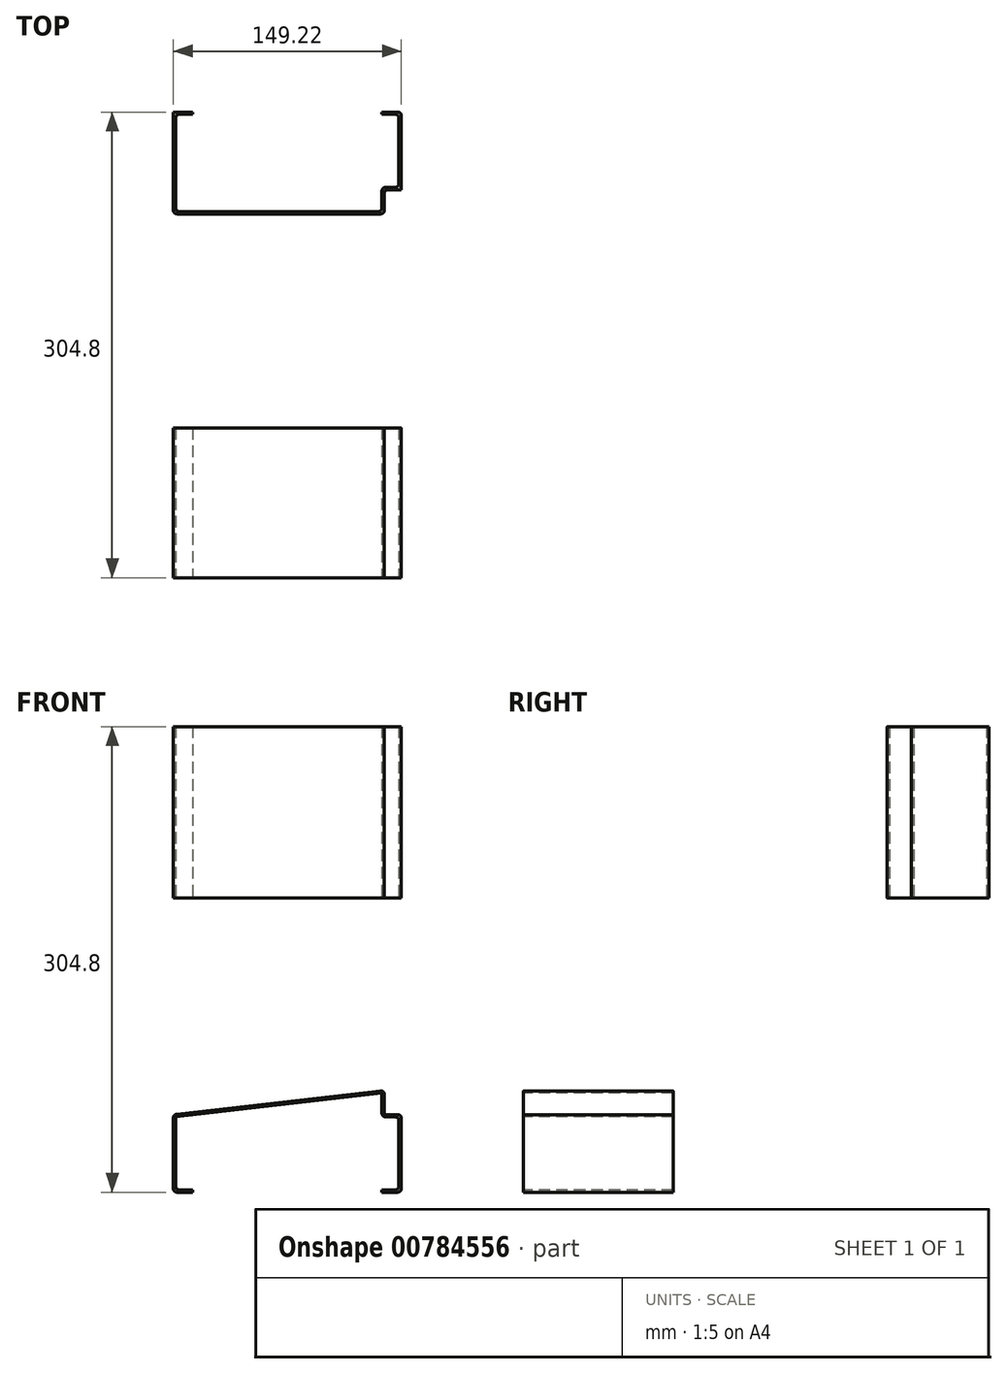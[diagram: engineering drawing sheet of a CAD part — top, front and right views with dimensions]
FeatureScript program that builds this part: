
annotation { "Feature Type Name" : "Feature", "Feature Type Description" : "" }
export const myFeature = defineFeature(function(context is Context, id is Id, definition is map)
    precondition{}
    {
        {
            var Q0;
            Q0=qCreatedBy(makeId("Front.planeOp"),FACE);
            var sketch = newSketch(context, id + "F0", { "sketchPlane" : qUnion([Q0])});
            skLineSegment(sketch, "E0", {"start": v(-61.91, -50.8) * mm, "end": v(-74.61, -50.8) * mm});
            skLineSegment(sketch, "E1", {"start": v(-74.61, -50.8) * mm, "end": v(-74.61, 0) * mm});
            skLineSegment(sketch, "E2", {"start": v(-74.61, 0) * mm, "end": v(63.5, 15.87) * mm});
            skLineSegment(sketch, "E3", {"start": v(63.5, 15.87) * mm, "end": v(63.5, 0) * mm});
            skLineSegment(sketch, "E4", {"start": v(63.5, 0) * mm, "end": v(74.61, 0) * mm});
            skLineSegment(sketch, "E5", {"start": v(74.61, 0) * mm, "end": v(74.61, -50.8) * mm});
            skLineSegment(sketch, "E6", {"start": v(74.61, -50.8) * mm, "end": v(61.91, -50.8) * mm});
            skLineSegment(sketch, "E7", {"start": v(-61.91, -50.8) * mm, "end": v(0, -50.8) * mm, "construction": true});
            skLineSegment(sketch, "E8", {"start": v(0, -50.8) * mm, "end": v(61.91, -50.8) * mm, "construction": true});
            skLineSegment(sketch, "E9.0", {"start": v(73.09, -49.28) * mm, "end": v(61.91, -49.28) * mm});
            skLineSegment(sketch, "E9.1", {"start": v(73.09, -1.52) * mm, "end": v(73.09, -49.28) * mm});
            skLineSegment(sketch, "E9.2", {"start": v(61.98, -1.52) * mm, "end": v(73.09, -1.52) * mm});
            skLineSegment(sketch, "E9.3", {"start": v(-61.91, -49.28) * mm, "end": v(-73.09, -49.28) * mm});
            skLineSegment(sketch, "E9.4", {"start": v(-73.09, -49.28) * mm, "end": v(-73.09, -1.36) * mm});
            skLineSegment(sketch, "E9.5", {"start": v(-73.09, -1.36) * mm, "end": v(61.98, 14.17) * mm});
            skLineSegment(sketch, "E9.6", {"start": v(61.98, 14.17) * mm, "end": v(61.98, -1.52) * mm});
            skLineSegment(sketch, "E10", {"start": v(-61.91, -49.28) * mm, "end": v(-61.91, -50.8) * mm});
            skLineSegment(sketch, "E11", {"start": v(61.91, -50.8) * mm, "end": v(61.91, -49.28) * mm});
            skSolve(sketch);
        }
        {
            var Q0;
            Q0=qSketchRegion(id+"F0",true);
            extrude(context, id + "F1", {"entities" : qUnion([Q0]), "oppositeDirection" : true, "depth" : 304.8 * mm, "offsetDistance" : 25.4 * mm});
        }
        {
            var Q0;
            Q0=qCreatedBy(makeId("Top.planeOp"),FACE);
            var sketch = newSketch(context, id + "F2", { "sketchPlane" : qUnion([Q0])});
            skPoint(sketch, "E12.0", {"position": v(-74.61, 304.8) * mm});
            skPoint(sketch, "E13.0", {"position": v(74.61, 304.8) * mm});
            skPoint(sketch, "E14.0", {"position": v(61.98, 304.8) * mm});
            skLineSegment(sketch, "E15", {"start": v(-74.61, 304.8) * mm, "end": v(-74.61, 238.12) * mm});
            skLineSegment(sketch, "E16", {"start": v(-74.61, 238.12) * mm, "end": v(63.5, 238.13) * mm});
            skLineSegment(sketch, "E17", {"start": v(63.5, 254) * mm, "end": v(74.61, 254) * mm});
            skLineSegment(sketch, "E18", {"start": v(74.61, 254) * mm, "end": v(74.61, 304.8) * mm});
            skLineSegment(sketch, "E19", {"start": v(61.98, 304.8) * mm, "end": v(74.61, 304.8) * mm});
            skLineSegment(sketch, "E20", {"start": v(-74.61, 304.8) * mm, "end": v(-61.91, 304.8) * mm});
            skLineSegment(sketch, "E21.0", {"start": v(-73.09, 303.28) * mm, "end": v(-61.91, 303.28) * mm});
            skLineSegment(sketch, "E21.1", {"start": v(-73.09, 303.28) * mm, "end": v(-73.09, 239.65) * mm});
            skLineSegment(sketch, "E21.2", {"start": v(-73.09, 239.65) * mm, "end": v(61.98, 239.65) * mm});
            skLineSegment(sketch, "E21.3", {"start": v(61.98, 303.28) * mm, "end": v(73.09, 303.28) * mm});
            skLineSegment(sketch, "E21.4", {"start": v(73.09, 255.52) * mm, "end": v(73.09, 303.28) * mm});
            skLineSegment(sketch, "E21.5", {"start": v(61.98, 255.52) * mm, "end": v(73.09, 255.52) * mm});
            skLineSegment(sketch, "E21.6", {"start": v(61.98, 239.65) * mm, "end": v(61.98, 255.52) * mm});
            skLineSegment(sketch, "E22", {"start": v(-61.91, 304.8) * mm, "end": v(-61.91, 303.28) * mm});
            skLineSegment(sketch, "E23", {"start": v(61.98, 304.8) * mm, "end": v(61.98, 303.28) * mm});
            skLineSegment(sketch, "E24", {"start": v(63.5, 238.13) * mm, "end": v(63.5, 254) * mm});
            skSolve(sketch);
        }
        {
            var Q0;
            Q0=qSketchRegion(id+"F2",true);
            extrude(context, id + "F3", {"entities" : qUnion([Q0]), "depth" : 254 * mm, "offsetDistance" : 25.4 * mm, "hasSecondDirection" : true, "secondDirectionOppositeDirection" : true, "secondDirectionDepth" : 50.8 * mm});
        }
        {
            var Q0;
            Q0=makeQuery(id+"F1.opExtrude","SWEPT_BODY",BODY,{"disambiguationData":[OSD([sQuery(id+"F0.wireOp",EDGE,"E0"),sQuery(id+"F0.wireOp",EDGE,"E1"),sQuery(id+"F0.wireOp",EDGE,"E2"),sQuery(id+"F0.wireOp",EDGE,"E3"),sQuery(id+"F0.wireOp",EDGE,"E4"),sQuery(id+"F0.wireOp",EDGE,"E5"),sQuery(id+"F0.wireOp",EDGE,"E6"),sQuery(id+"F0.wireOp",EDGE,"E9.0"),sQuery(id+"F0.wireOp",EDGE,"E9.1"),sQuery(id+"F0.wireOp",EDGE,"E9.2"),sQuery(id+"F0.wireOp",EDGE,"E9.3"),sQuery(id+"F0.wireOp",EDGE,"E9.4"),sQuery(id+"F0.wireOp",EDGE,"E9.5"),sQuery(id+"F0.wireOp",EDGE,"E9.6"),sQuery(id+"F0.wireOp",EDGE,"E10"),sQuery(id+"F0.wireOp",EDGE,"E11")])]});
            var Q1;
            Q1=makeQuery(id+"F3.opExtrude","SWEPT_BODY",BODY,{"disambiguationData":[OSD([sQuery(id+"F2.wireOp",EDGE,"E15"),sQuery(id+"F2.wireOp",EDGE,"E16"),sQuery(id+"F2.wireOp",EDGE,"vNE0MKmX-Wy9i-YOhV-lQRx-KuhJFtJfketY"),sQuery(id+"F2.wireOp",EDGE,"E17"),sQuery(id+"F2.wireOp",EDGE,"E18"),sQuery(id+"F2.wireOp",EDGE,"E19"),sQuery(id+"F2.wireOp",EDGE,"E20"),sQuery(id+"F2.wireOp",EDGE,"E21.0"),sQuery(id+"F2.wireOp",EDGE,"E21.1"),sQuery(id+"F2.wireOp",EDGE,"E21.2"),sQuery(id+"F2.wireOp",EDGE,"E21.3"),sQuery(id+"F2.wireOp",EDGE,"E21.4"),sQuery(id+"F2.wireOp",EDGE,"E21.5"),sQuery(id+"F2.wireOp",EDGE,"E21.6"),sQuery(id+"F2.wireOp",EDGE,"E22"),sQuery(id+"F2.wireOp",EDGE,"E23")])]});
            booleanBodies(context, id + "F4", {"operationType" : BooleanOperationType.INTERSECTION, "tools" : qUnion([Q0, Q1]), "keepTools" : true});
        }
        {
            var Q0;
            Q0=makeQuery(id+"F3.opExtrude","SWEPT_FACE",FACE,{"disambiguationData":[OSD([sQuery(id+"F2.wireOp",EDGE,"E16")])]});
            var sketch = newSketch(context, id + "F5", { "sketchPlane" : qUnion([Q0])});
            skPoint(sketch, "E25.0", {"position": v(61.98, 14.17) * mm});
            skPoint(sketch, "E26.0", {"position": v(-73.09, -1.36) * mm});
            skLineSegment(sketch, "E27", {"start": v(-73.09, -1.36) * mm, "end": v(61.98, 14.17) * mm});
            skLineSegment(sketch, "E28", {"start": v(-73.09, -1.36) * mm, "end": v(-91.14, -3.43) * mm});
            skPoint(sketch, "E29.0", {"position": v(61.98, 0) * mm});
            skLineSegment(sketch, "E30", {"start": v(61.98, 14.17) * mm, "end": v(61.98, 0) * mm});
            skLineSegment(sketch, "E31", {"start": v(61.98, 0) * mm, "end": v(86.32, 0) * mm});
            skLineSegment(sketch, "E32", {"start": v(-91.14, -3.43) * mm, "end": v(-91.14, -71.1) * mm});
            skLineSegment(sketch, "E33", {"start": v(-91.14, -71.1) * mm, "end": v(86.32, -71.1) * mm});
            skLineSegment(sketch, "E34", {"start": v(86.32, -71.1) * mm, "end": v(86.32, 0) * mm});
            skPoint(sketch, "E35.0", {"position": v(63.5, 0) * mm});
            skSolve(sketch);
        }
        {
            var Q0;
            Q0=qSketchRegion(id+"F5",true);
            var Q1;
            Q1=makeQuery(id+"F3.opExtrude","SWEPT_FACE",FACE,{"disambiguationData":[OSD([sQuery(id+"F2.wireOp",EDGE,"E17")])]});
            extrude(context, id + "F6", {"entities" : qUnion([Q0]), "operationType" : NewBodyOperationType.REMOVE, "endBound" : BoundingType.UP_TO_SURFACE, "oppositeDirection" : true, "depth" : 25.4 * mm, "endBoundEntityFace" : qUnion([Q1]), "offsetDistance" : 25.4 * mm});
        }
        {
            var Q0;
            Q0=makeQuery(id+"F3.opExtrude","SWEPT_FACE",FACE,{"disambiguationData":[OSD([sQuery(id+"F2.wireOp",EDGE,"E16")])]});
            var sketch = newSketch(context, id + "F7", { "sketchPlane" : qUnion([Q0])});
            skPoint(sketch, "E36.0", {"position": v(-74.61, -1.53) * mm});
            skPoint(sketch, "E37.0", {"position": v(63.5, 0) * mm});
            skPoint(sketch, "E38.0", {"position": v(61.98, 0) * mm});
            skPoint(sketch, "E39.0", {"position": v(63.5, 15.87) * mm});
            skPoint(sketch, "E40.0", {"position": v(-74.61, 0) * mm});
            skPoint(sketch, "E41.0", {"position": v(-73.09, -1.36) * mm});
            skPoint(sketch, "E42.0", {"position": v(61.98, 14.17) * mm});
            skLineSegment(sketch, "E43", {"start": v(-74.61, -1.53) * mm, "end": v(61.98, 14.17) * mm});
            skLineSegment(sketch, "E44", {"start": v(61.98, 14.17) * mm, "end": v(61.98, 0) * mm});
            skLineSegment(sketch, "E45", {"start": v(61.98, 0) * mm, "end": v(63.5, 0) * mm});
            skLineSegment(sketch, "E46", {"start": v(63.5, 0) * mm, "end": v(63.5, 15.87) * mm});
            skLineSegment(sketch, "E47", {"start": v(63.5, 15.87) * mm, "end": v(-74.61, 0) * mm});
            skLineSegment(sketch, "E48", {"start": v(-74.61, 0) * mm, "end": v(-74.61, -1.53) * mm});
            skSolve(sketch);
        }
        {
            var Q0;
            Q0=qSketchRegion(id+"F7",true);
            extrude(context, id + "F8", {"entities" : qUnion([Q0]), "operationType" : NewBodyOperationType.REMOVE, "endBound" : BoundingType.THROUGH_ALL, "oppositeDirection" : true, "depth" : 25.4 * mm, "offsetDistance" : 25.4 * mm});
        }
        {
            var Q0;
            Q0=makeQuery(id+"F4.opBoolean","INTERSECT",BODY,{"derivedFrom":[makeQuery(id+"F1.opExtrude","SWEPT_BODY",BODY,{"disambiguationData":[OSD([sQuery(id+"F0.wireOp",EDGE,"E0"),sQuery(id+"F0.wireOp",EDGE,"E1"),sQuery(id+"F0.wireOp",EDGE,"E2"),sQuery(id+"F0.wireOp",EDGE,"E3"),sQuery(id+"F0.wireOp",EDGE,"E4"),sQuery(id+"F0.wireOp",EDGE,"E5"),sQuery(id+"F0.wireOp",EDGE,"E6"),sQuery(id+"F0.wireOp",EDGE,"E9.0"),sQuery(id+"F0.wireOp",EDGE,"E9.1"),sQuery(id+"F0.wireOp",EDGE,"E9.2"),sQuery(id+"F0.wireOp",EDGE,"E9.3"),sQuery(id+"F0.wireOp",EDGE,"E9.4"),sQuery(id+"F0.wireOp",EDGE,"E9.5"),sQuery(id+"F0.wireOp",EDGE,"E9.6"),sQuery(id+"F0.wireOp",EDGE,"E10"),sQuery(id+"F0.wireOp",EDGE,"E11")])]}),makeQuery(id+"F3.opExtrude","SWEPT_BODY",BODY,{"disambiguationData":[OSD([sQuery(id+"F2.wireOp",EDGE,"E15"),sQuery(id+"F2.wireOp",EDGE,"E16"),sQuery(id+"F2.wireOp",EDGE,"E17"),sQuery(id+"F2.wireOp",EDGE,"E18"),sQuery(id+"F2.wireOp",EDGE,"E19"),sQuery(id+"F2.wireOp",EDGE,"E20"),sQuery(id+"F2.wireOp",EDGE,"E21.0"),sQuery(id+"F2.wireOp",EDGE,"E21.1"),sQuery(id+"F2.wireOp",EDGE,"E21.2"),sQuery(id+"F2.wireOp",EDGE,"E21.3"),sQuery(id+"F2.wireOp",EDGE,"E21.4"),sQuery(id+"F2.wireOp",EDGE,"E21.5"),sQuery(id+"F2.wireOp",EDGE,"E21.6"),sQuery(id+"F2.wireOp",EDGE,"E22"),sQuery(id+"F2.wireOp",EDGE,"E23"),sQuery(id+"F2.wireOp",EDGE,"E24")])]})]});
            deleteBodies(context, id + "F9", {"entities" : qUnion([Q0])});
        }
        {
            var Q0;
            Q0=makeQuery(id+"F1.opExtrude","SWEPT_BODY",BODY,{"disambiguationData":[OSD([sQuery(id+"F0.wireOp",EDGE,"E0"),sQuery(id+"F0.wireOp",EDGE,"E1"),sQuery(id+"F0.wireOp",EDGE,"E2"),sQuery(id+"F0.wireOp",EDGE,"E3"),sQuery(id+"F0.wireOp",EDGE,"E4"),sQuery(id+"F0.wireOp",EDGE,"E5"),sQuery(id+"F0.wireOp",EDGE,"E6"),sQuery(id+"F0.wireOp",EDGE,"E9.0"),sQuery(id+"F0.wireOp",EDGE,"E9.1"),sQuery(id+"F0.wireOp",EDGE,"E9.2"),sQuery(id+"F0.wireOp",EDGE,"E9.3"),sQuery(id+"F0.wireOp",EDGE,"E9.4"),sQuery(id+"F0.wireOp",EDGE,"E9.5"),sQuery(id+"F0.wireOp",EDGE,"E9.6"),sQuery(id+"F0.wireOp",EDGE,"E10"),sQuery(id+"F0.wireOp",EDGE,"E11")])]});
            var Q1;
            Q1=makeQuery(id+"F3.opExtrude","SWEPT_BODY",BODY,{"disambiguationData":[OSD([sQuery(id+"F2.wireOp",EDGE,"E15"),sQuery(id+"F2.wireOp",EDGE,"E16"),sQuery(id+"F2.wireOp",EDGE,"E17"),sQuery(id+"F2.wireOp",EDGE,"E18"),sQuery(id+"F2.wireOp",EDGE,"E19"),sQuery(id+"F2.wireOp",EDGE,"E20"),sQuery(id+"F2.wireOp",EDGE,"E21.0"),sQuery(id+"F2.wireOp",EDGE,"E21.1"),sQuery(id+"F2.wireOp",EDGE,"E21.2"),sQuery(id+"F2.wireOp",EDGE,"E21.3"),sQuery(id+"F2.wireOp",EDGE,"E21.4"),sQuery(id+"F2.wireOp",EDGE,"E21.5"),sQuery(id+"F2.wireOp",EDGE,"E21.6"),sQuery(id+"F2.wireOp",EDGE,"E22"),sQuery(id+"F2.wireOp",EDGE,"E23"),sQuery(id+"F2.wireOp",EDGE,"E24")])]});
            booleanBodies(context, id + "F10", {"operationType" : BooleanOperationType.UNION, "tools" : qUnion([Q0, Q1])});
        }
        {
            var Q0;
            {var subQ0=sQuery(id+"F0.wireOp",EDGE,"E3");var subQ2=sQuery(id+"F0.wireOp",EDGE,"E4");Q0=makeQuery(id+"F10.opBoolean","SPLIT",FACE,{"disambiguationData":[TD([makeQuery(id+"F1.opExtrude","SWEPT_FACE",FACE,{"disambiguationData":[OSD([subQ0])]})])],"derivedFrom":makeQuery(id+"F8.boolean.opBoolean","MERGE",FACE,{"derivedFrom":[makeQuery(id+"F1.opExtrude","SWEPT_FACE",FACE,{"disambiguationData":[OSD([subQ2])]})],"fromTools":[makeQuery(id+"F8.opExtrude","SWEPT_FACE",FACE,{"disambiguationData":[OSD([sQuery(id+"F7.wireOp",EDGE,"E45")])]})]})});}
            var sketch = newSketch(context, id + "F11", { "sketchPlane" : qUnion([Q0])});
            skPoint(sketch, "E49.0", {"position": v(63.5, 238.13) * mm});
            skLineSegment(sketch, "E50.bottom", {"start": v(63.5, 238.13) * mm, "end": v(61.37, 238.13) * mm});
            skLineSegment(sketch, "E50.top", {"start": v(63.5, 238.07) * mm, "end": v(61.37, 238.07) * mm});
            skLineSegment(sketch, "E50.left", {"start": v(63.5, 238.13) * mm, "end": v(63.5, 238.07) * mm});
            skLineSegment(sketch, "E50.right", {"start": v(61.37, 238.13) * mm, "end": v(61.37, 238.07) * mm});
            skSolve(sketch);
        }
        {
            var Q0;
            Q0=qSketchRegion(id+"F11",true);
            extrude(context, id + "F12", {"entities" : qUnion([Q0]), "operationType" : NewBodyOperationType.REMOVE, "endBound" : BoundingType.THROUGH_ALL, "depth" : 25.4 * mm, "offsetDistance" : 25.4 * mm});
        }
        {
            var Q0;
            Q0=qCreatedBy(makeId("Right.planeOp"),FACE);
            var sketch = newSketch(context, id + "F13", { "sketchPlane" : qUnion([Q0])});
            skLineSegment(sketch, "E51.bottom", {"start": v(97.94, 141.78) * mm, "end": v(397.03, 141.78) * mm});
            skLineSegment(sketch, "E51.top", {"start": v(97.94, -138.25) * mm, "end": v(397.03, -138.25) * mm});
            skLineSegment(sketch, "E51.left", {"start": v(97.94, 141.78) * mm, "end": v(97.94, -138.25) * mm});
            skLineSegment(sketch, "E51.right", {"start": v(397.03, 141.78) * mm, "end": v(397.03, -138.25) * mm});
            skSolve(sketch);
        }
        {
            var Q0;
            Q0 = qSketchRegion(id + "F13", true);
            extrude(context, id + "F14", {"entities" : qUnion([Q0]), "operationType" : NewBodyOperationType.REMOVE, "endBound" : BoundingType.THROUGH_ALL, "oppositeDirection" : true, "depth" : 25.4 * mm, "offsetDistance" : 25.4 * mm, "hasSecondDirection" : true, "secondDirectionBound" : BoundingType.THROUGH_ALL, "secondDirectionOppositeDirection" : false, "secondDirectionDepth" : 25.4 * mm});
        }
        {
            var Q0;
            Q0=makeQuery(id+"F3.opExtrude","SWEPT_EDGE",EDGE,{"disambiguationData":[OSD([sQuery(id+"F2.wireOp",EDGE,"E21.1"),sQuery(id+"F2.wireOp",EDGE,"E21.2")])]});
            var Q1;
            Q1=makeQuery(id+"F3.opExtrude","SWEPT_EDGE",EDGE,{"disambiguationData":[OSD([sQuery(id+"F2.wireOp",EDGE,"E15"),sQuery(id+"F2.wireOp",EDGE,"E16")])]});
            var Q2;
            Q2=makeQuery(id+"F10.opBoolean","MERGE",EDGE,{"derivedFrom":[makeQuery(id+"F3.opExtrude","SWEPT_EDGE",EDGE,{"disambiguationData":[OSD([sQuery(id+"F2.wireOp",EDGE,"E15"),sQuery(id+"F2.wireOp",EDGE,"E20")])]}),makeQuery(id+"F1.opExtrude","CAP_EDGE",EDGE,{"disambiguationData":[OSD([sQuery(id+"F0.wireOp",EDGE,"E1")])],"isStart":false})]});
            var Q3;
            Q3=makeQuery(id+"F3.opExtrude","SWEPT_EDGE",EDGE,{"disambiguationData":[OSD([sQuery(id+"F2.wireOp",EDGE,"E21.0"),sQuery(id+"F2.wireOp",EDGE,"E21.1")])]});
            var Q4;
            Q4=makeQuery(id+"F3.opExtrude","SWEPT_EDGE",EDGE,{"disambiguationData":[OSD([sQuery(id+"F2.wireOp",EDGE,"E21.2"),sQuery(id+"F2.wireOp",EDGE,"E21.6")])]});
            var Q5;
            {var subQ1=sQuery(id+"F2.wireOp",EDGE,"E21.6");var subQ2=sQuery(id+"F2.wireOp",EDGE,"E21.5");Q5=makeQuery(id+"F10.opBoolean","SPLIT",EDGE,{"disambiguationData":[TD([makeQuery(id+"F1.opExtrude","SWEPT_FACE",FACE,{"disambiguationData":[OSD([sQuery(id+"F0.wireOp",EDGE,"E4")])]})])],"derivedFrom":makeQuery(id+"F3.opExtrude","SWEPT_EDGE",EDGE,{"disambiguationData":[OSD([subQ2,subQ1])]})});}
            var Q6;
            {var subQ0=sQuery(id+"F2.wireOp",EDGE,"E21.4");var subQ1=sQuery(id+"F2.wireOp",EDGE,"E21.5");Q6=makeQuery(id+"F10.opBoolean","SPLIT",EDGE,{"disambiguationData":[topologyDisambiguationEdgeConnected([makeQuery(id+"F3.opExtrude","SWEPT_FACE",FACE,{"disambiguationData":[OSD([subQ0])]})])],"derivedFrom":makeQuery(id+"F3.opExtrude","SWEPT_EDGE",EDGE,{"disambiguationData":[OSD([subQ0,subQ1])]})});}
            var Q7;
            {var subQ0=sQuery(id+"F2.wireOp",EDGE,"E21.3");var subQ1=sQuery(id+"F2.wireOp",EDGE,"E21.4");Q7=makeQuery(id+"F10.opBoolean","SPLIT",EDGE,{"disambiguationData":[topologyDisambiguationEdgeConnected([makeQuery(id+"F3.opExtrude","SWEPT_FACE",FACE,{"disambiguationData":[OSD([subQ1])]})])],"derivedFrom":makeQuery(id+"F3.opExtrude","SWEPT_EDGE",EDGE,{"disambiguationData":[OSD([subQ0,subQ1])]})});}
            var Q8;
            {var subQ0=sQuery(id+"F2.wireOp",EDGE,"E24");Q8=makeQuery(id+"F12.boolean.opBoolean","MERGE",EDGE,{"derivedFrom":[makeQuery(id+"F3.opExtrude","SWEPT_EDGE",EDGE,{"disambiguationData":[OSD([sQuery(id+"F2.wireOp",EDGE,"E16"),subQ0])]})],"fromTools":[makeQuery(id+"F12.opExtrude","SWEPT_EDGE",EDGE,{"disambiguationData":[OSD([sQuery(id+"F0.wireOp",EDGE,"E3"),sQuery(id+"F0.wireOp",EDGE,"E4"),subQ0,sQuery(id+"F5.wireOp",EDGE,"E31"),sQuery(id+"F11.wireOp",EDGE,"E50.bottom"),sQuery(id+"F11.wireOp",EDGE,"E50.left")])]})]});}
            var Q9;
            Q9=makeQuery(id+"F3.opExtrude","SWEPT_EDGE",EDGE,{"disambiguationData":[OSD([sQuery(id+"F2.wireOp",EDGE,"E17"),sQuery(id+"F2.wireOp",EDGE,"E24")])]});
            var Q10;
            Q10=makeQuery(id+"F3.opExtrude","SWEPT_EDGE",EDGE,{"disambiguationData":[OSD([sQuery(id+"F2.wireOp",EDGE,"E17"),sQuery(id+"F2.wireOp",EDGE,"E18")])]});
            var Q11;
            Q11=makeQuery(id+"F10.opBoolean","MERGE",EDGE,{"derivedFrom":[makeQuery(id+"F1.opExtrude","CAP_EDGE",EDGE,{"disambiguationData":[OSD([sQuery(id+"F0.wireOp",EDGE,"E5")])],"isStart":false}),makeQuery(id+"F3.opExtrude","SWEPT_EDGE",EDGE,{"disambiguationData":[OSD([sQuery(id+"F2.wireOp",EDGE,"E18"),sQuery(id+"F2.wireOp",EDGE,"E19")])]})]});
            fillet(context, id + "F15", {"entities" : qUnion([Q0, Q1, Q2, Q3, Q4, Q5, Q6, Q7, Q8, Q9, Q10, Q11]), "radius" : 2.38 * mm, "tangentPropagation" : true, "allowEdgeOverflow" : false});
        }
        {
            var Q0;
            Q0=makeQuery(id+"F1.opExtrude","SWEPT_EDGE",EDGE,{"disambiguationData":[OSD([sQuery(id+"F0.wireOp",EDGE,"E9.3"),sQuery(id+"F0.wireOp",EDGE,"E9.4")])]});
            var Q1;
            {var subQ0=sQuery(id+"F0.wireOp",EDGE,"E9.4");var subQ2=sQuery(id+"F0.wireOp",EDGE,"E9.5");var subQ3=makeQuery(id+"F1.opExtrude","SWEPT_EDGE",EDGE,{"disambiguationData":[OSD([subQ0,subQ2])]});Q1=makeQuery(id+"F10.opBoolean","MERGE",EDGE,{"derivedFrom":[makeQuery(id+"F8.boolean.opBoolean","SPLIT",EDGE,{"disambiguationData":[topologyDisambiguationEdgeConnected([makeQuery(id+"F1.opExtrude","SWEPT_FACE",FACE,{"disambiguationData":[OSD([subQ2])]})])],"derivedFrom":subQ3}),makeQuery(id+"F8.boolean.opBoolean","SPLIT",EDGE,{"disambiguationData":[topologyDisambiguationEdgeConnected([makeQuery(id+"F8.opExtrude","SWEPT_FACE",FACE,{"disambiguationData":[OSD([sQuery(id+"F7.wireOp",EDGE,"E43")])]})])],"derivedFrom":subQ3})]});}
            var Q2;
            {var subQ0=sQuery(id+"F0.wireOp",EDGE,"E9.6");var subQ1=sQuery(id+"F0.wireOp",EDGE,"E9.5");var subQ2=sQuery(id+"F5.wireOp",EDGE,"E27");Q2=makeQuery(id+"F12.boolean.opBoolean","SPLIT",EDGE,{"disambiguationData":[TD([makeQuery(id+"F12.opExtrude","SWEPT_FACE",FACE,{"disambiguationData":[OSD([sQuery(id+"F11.wireOp",EDGE,"E50.top")])]})])],"derivedFrom":makeQuery(id+"F10.opBoolean","MERGE",EDGE,{"derivedFrom":[makeQuery(id+"F6.boolean.opBoolean","COPY",EDGE,{"derivedFrom":makeQuery(id+"F6.opExtrude","SWEPT_EDGE",EDGE,{"disambiguationData":[OSD([subQ2,sQuery(id+"F5.wireOp",EDGE,"E30")])]})}),makeQuery(id+"F1.opExtrude","SWEPT_EDGE",EDGE,{"disambiguationData":[OSD([subQ1,subQ0])]})]})});}
            var Q3;
            {var subQ0=sQuery(id+"F0.wireOp",EDGE,"E9.6");var subQ1=sQuery(id+"F0.wireOp",EDGE,"E9.2");Q3=makeQuery(id+"F10.opBoolean","SPLIT",EDGE,{"disambiguationData":[TD([makeQuery(id+"F3.opExtrude","SWEPT_FACE",FACE,{"disambiguationData":[OSD([sQuery(id+"F2.wireOp",EDGE,"E17")])]})])],"derivedFrom":makeQuery(id+"F1.opExtrude","SWEPT_EDGE",EDGE,{"disambiguationData":[OSD([subQ1,subQ0])]})});}
            var Q4;
            {var subQ0=sQuery(id+"F0.wireOp",EDGE,"E9.2");var subQ1=sQuery(id+"F0.wireOp",EDGE,"E9.1");Q4=makeQuery(id+"F10.opBoolean","SPLIT",EDGE,{"disambiguationData":[TD([makeQuery(id+"F3.opExtrude","SWEPT_FACE",FACE,{"disambiguationData":[OSD([sQuery(id+"F2.wireOp",EDGE,"E17")])]})])],"derivedFrom":makeQuery(id+"F1.opExtrude","SWEPT_EDGE",EDGE,{"disambiguationData":[OSD([subQ1,subQ0])]})});}
            var Q5;
            {var subQ0=sQuery(id+"F0.wireOp",EDGE,"E9.1");var subQ1=sQuery(id+"F0.wireOp",EDGE,"E9.0");Q5=makeQuery(id+"F10.opBoolean","SPLIT",EDGE,{"disambiguationData":[TD([makeQuery(id+"F3.opExtrude","SWEPT_FACE",FACE,{"disambiguationData":[OSD([sQuery(id+"F2.wireOp",EDGE,"E17")])]})])],"derivedFrom":makeQuery(id+"F1.opExtrude","SWEPT_EDGE",EDGE,{"disambiguationData":[OSD([subQ1,subQ0])]})});}
            var Q6;
            Q6=makeQuery(id+"F1.opExtrude","SWEPT_EDGE",EDGE,{"disambiguationData":[OSD([sQuery(id+"F0.wireOp",EDGE,"E5"),sQuery(id+"F0.wireOp",EDGE,"E6")])]});
            var Q7;
            Q7=makeQuery(id+"F1.opExtrude","SWEPT_EDGE",EDGE,{"disambiguationData":[OSD([sQuery(id+"F0.wireOp",EDGE,"E4"),sQuery(id+"F0.wireOp",EDGE,"E5")])]});
            var Q8;
            Q8=makeQuery(id+"F1.opExtrude","SWEPT_EDGE",EDGE,{"disambiguationData":[OSD([sQuery(id+"F0.wireOp",EDGE,"E2"),sQuery(id+"F0.wireOp",EDGE,"E3")])]});
            var Q9;
            Q9=makeQuery(id+"F1.opExtrude","SWEPT_EDGE",EDGE,{"disambiguationData":[OSD([sQuery(id+"F0.wireOp",EDGE,"E1"),sQuery(id+"F0.wireOp",EDGE,"E2")])]});
            var Q10;
            Q10=makeQuery(id+"F1.opExtrude","SWEPT_EDGE",EDGE,{"disambiguationData":[OSD([sQuery(id+"F0.wireOp",EDGE,"E0"),sQuery(id+"F0.wireOp",EDGE,"E1")])]});
            var Q11;
            {var subQ0=makeQuery(id+"F3.opExtrude","SWEPT_FACE",FACE,{"disambiguationData":[OSD([sQuery(id+"F2.wireOp",EDGE,"E24")])]});var subQ1=sQuery(id+"F0.wireOp",EDGE,"E3");var subQ2=sQuery(id+"F11.wireOp",EDGE,"E50.top");var subQ3=sQuery(id+"F0.wireOp",EDGE,"E4");Q11=makeQuery(id+"F12.boolean.opBoolean","SPLIT",EDGE,{"disambiguationData":[TD([makeQuery(id+"F12.opExtrude","SWEPT_FACE",FACE,{"disambiguationData":[OSD([subQ2])]})])],"derivedFrom":makeQuery(id+"F10.opBoolean","MERGE",EDGE,{"derivedFrom":[makeQuery(id+"F6.boolean.opBoolean","INTERSECT",EDGE,{"derivedFrom":[subQ0,makeQuery(id+"F6.opExtrude","SWEPT_FACE",FACE,{"disambiguationData":[OSD([sQuery(id+"F5.wireOp",EDGE,"E31")])]})]}),makeQuery(id+"F1.opExtrude","SWEPT_EDGE",EDGE,{"disambiguationData":[OSD([subQ1,subQ3])]})]})});}
            fillet(context, id + "F16", {"entities" : qUnion([Q0, Q1, Q2, Q3, Q4, Q5, Q6, Q7, Q8, Q9, Q10, Q11]), "radius" : 2.38 * mm, "tangentPropagation" : true, "allowEdgeOverflow" : false});
        }
    });
